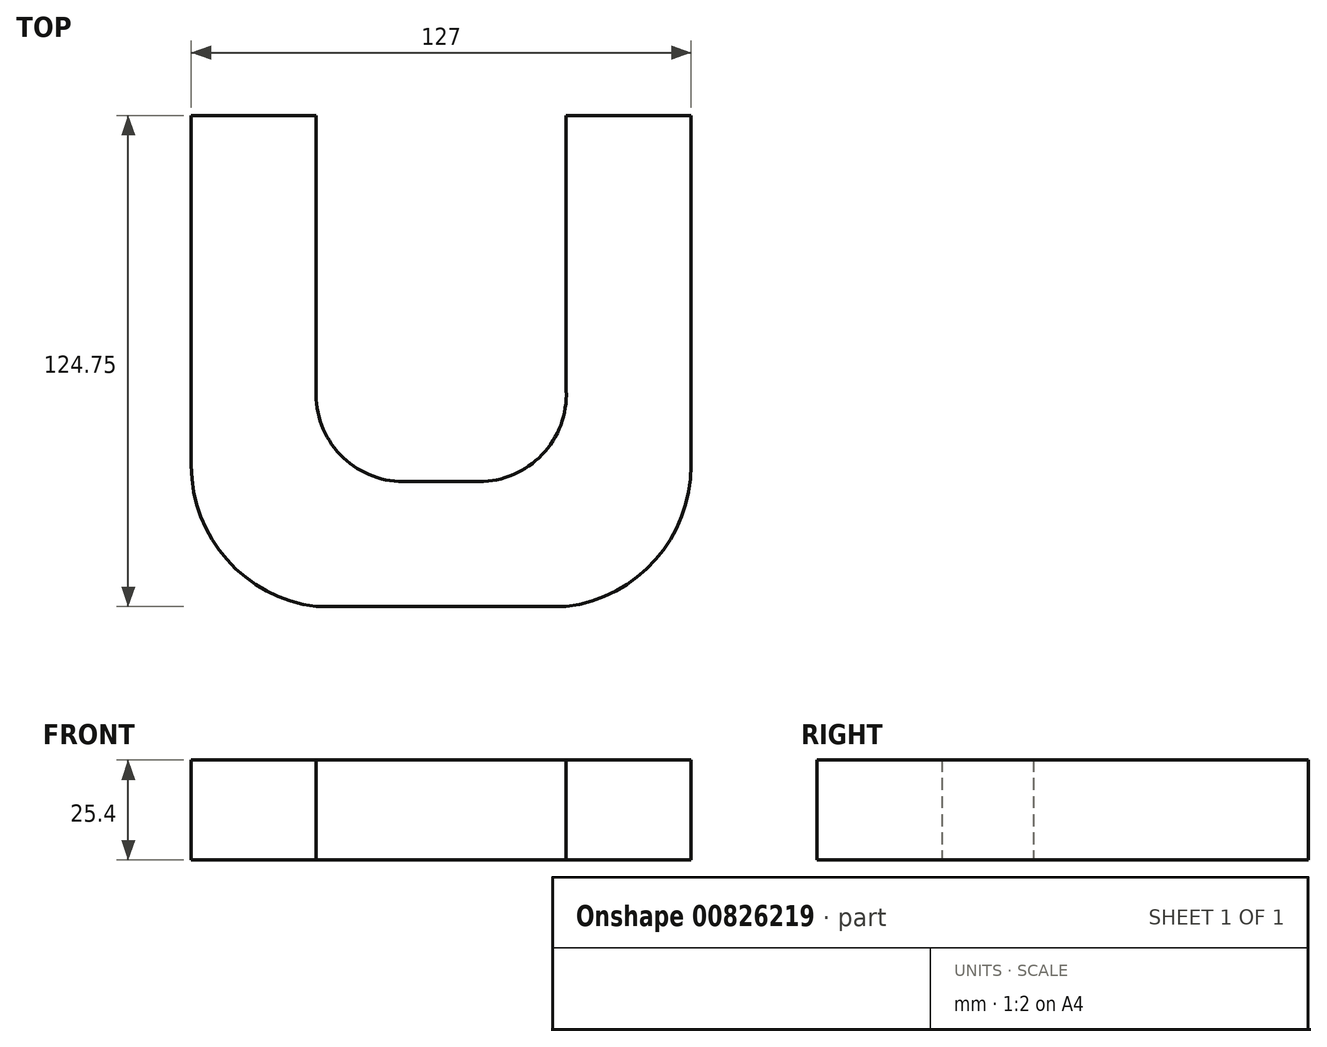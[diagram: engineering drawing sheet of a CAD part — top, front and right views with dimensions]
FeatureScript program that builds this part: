
annotation { "Feature Type Name" : "Feature", "Feature Type Description" : "" }
export const myFeature = defineFeature(function(context is Context, id is Id, definition is map)
    precondition{}
    {
        {
            var Q0;
            Q0=qCreatedBy(makeId("Top.planeOp"),FACE);
            var sketch = newSketch(context, id + "F0", { "sketchPlane" : qUnion([Q0])});
            skLineSegment(sketch, "E0", {"start": v(-54.25, -49.9) * mm, "end": v(9.25, -49.9) * mm, "construction": true});
            skLineSegment(sketch, "E1", {"start": v(-32.16, -73.05) * mm, "end": v(-12.85, -73.05) * mm});
            skArc(sketch, "E2", {"start": v(-54.25, -49.9) * mm, "mid": v(-48.16, -66.2) * mm, "end": v(-32.16, -73.05) * mm});
            skArc(sketch, "E3", {"start": v(-12.85, -73.05) * mm, "mid": v(3.15, -66.2) * mm, "end": v(9.25, -49.9) * mm});
            skLineSegment(sketch, "E4", {"start": v(-54.25, -49.9) * mm, "end": v(-54.25, -104.8) * mm, "construction": true});
            skLineSegment(sketch, "E5", {"start": v(-54.25, -104.8) * mm, "end": v(9.25, -104.8) * mm});
            skLineSegment(sketch, "E6", {"start": v(9.25, -104.8) * mm, "end": v(9.25, -49.9) * mm, "construction": true});
            skLineSegment(sketch, "E7", {"start": v(-86, -68.95) * mm, "end": v(-86, 19.95) * mm});
            skLineSegment(sketch, "E8", {"start": v(41, -68.95) * mm, "end": v(41, 19.95) * mm});
            skLineSegment(sketch, "E9", {"start": v(-54.25, 19.95) * mm, "end": v(9.25, 19.95) * mm, "construction": true});
            skLineSegment(sketch, "E10", {"start": v(-54.25, -49.9) * mm, "end": v(-54.25, 19.95) * mm});
            skLineSegment(sketch, "E11", {"start": v(9.25, -49.9) * mm, "end": v(9.25, 19.95) * mm});
            skPoint(sketch, "E11.endSnap0", {"position": v(-22.5, 19.95) * mm});
            skLineSegment(sketch, "E12", {"start": v(-54.25, 19.95) * mm, "end": v(-86, 19.95) * mm});
            skLineSegment(sketch, "E13", {"start": v(9.25, 19.95) * mm, "end": v(41, 19.95) * mm});
            skArc(sketch, "E14", {"start": v(-86, -68.95) * mm, "mid": v(-76.92, -92.9) * mm, "end": v(-54.25, -104.8) * mm});
            skArc(sketch, "E15", {"start": v(9.25, -104.8) * mm, "mid": v(31.92, -92.9) * mm, "end": v(41, -68.95) * mm});
            skSolve(sketch);
        }
        {
            var Q0;
            Q0=makeQuery(id+"F0.imprint","IMPRINT",FACE,{"disambiguationData":[TD([[makeQuery(id+"F0.imprint","IMPRINT",EDGE,{"derivedFrom":sQuery(id+"F0.wireOp",EDGE,"E1")}),-1.0]])]});
            extrude(context, id + "F1", {"entities" : qUnion([Q0]), "depth" : 25.4 * mm, "offsetDistance" : 25.4 * mm});
        }
    });
